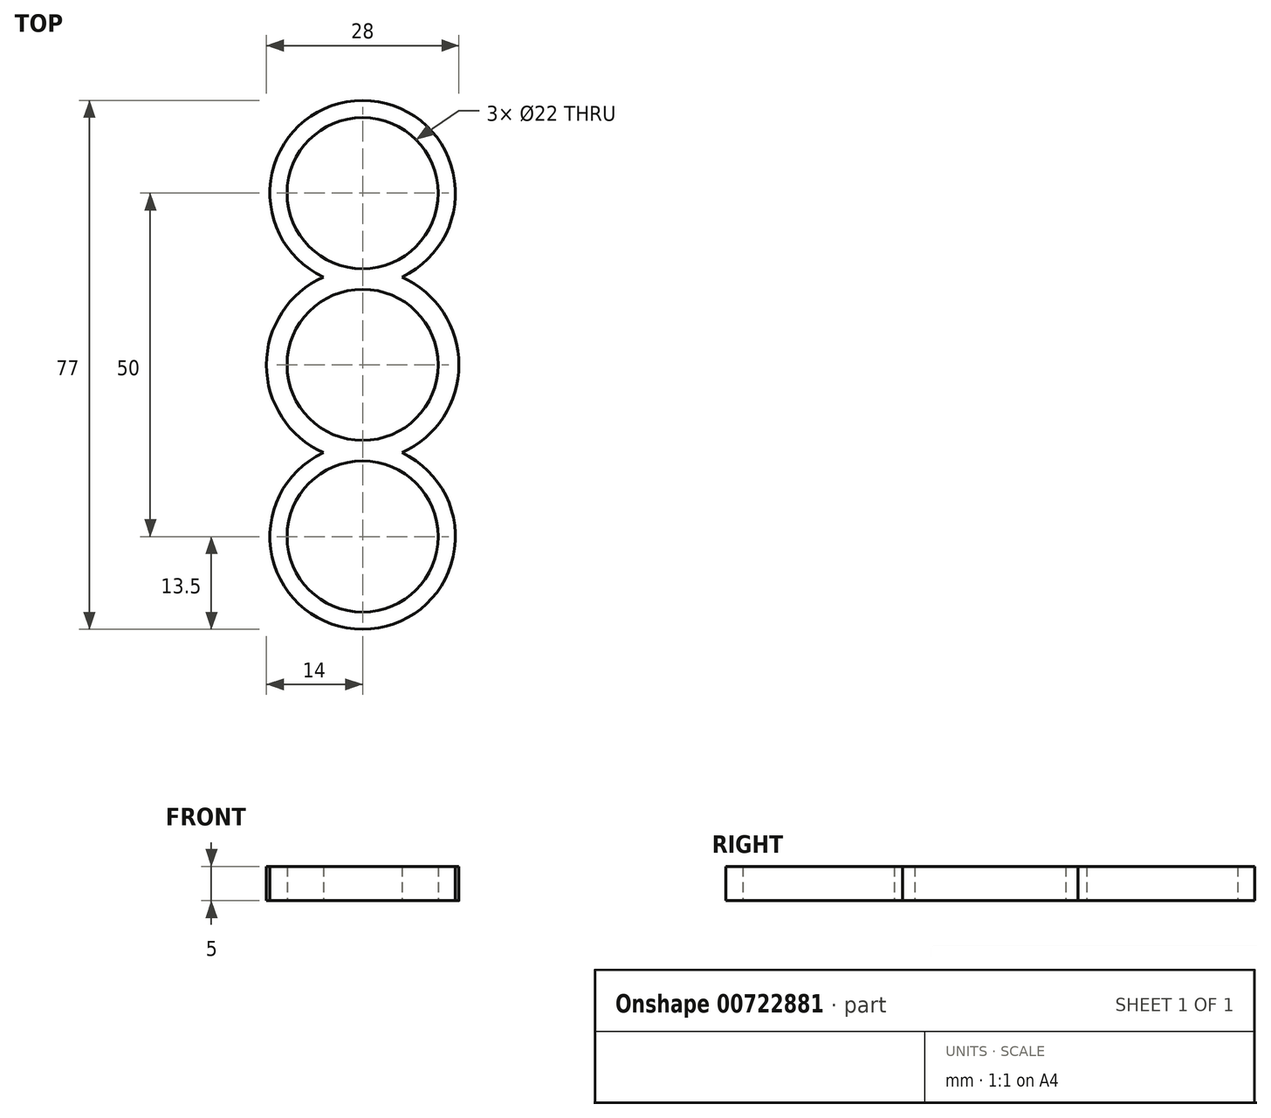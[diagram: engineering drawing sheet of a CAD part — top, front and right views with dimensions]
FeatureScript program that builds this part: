
annotation { "Feature Type Name" : "Feature", "Feature Type Description" : "" }
export const myFeature = defineFeature(function(context is Context, id is Id, definition is map)
    precondition{}
    {
        {
            var Q0;
            Q0=qCreatedBy(makeId("Top.planeOp"),FACE);
            var sketch = newSketch(context, id + "F0", { "sketchPlane" : qUnion([Q0])});
            skCircle(sketch, "E0", {"center": v(0, 0) * mm, "radius": 11 * mm});
            skLineSegment(sketch, "E1", {"start": v(0, 11) * mm, "end": v(0, 14) * mm});
            skCircle(sketch, "E2", {"center": v(0, 25) * mm, "radius": 11 * mm});
            skArc(sketch, "E3", {"start": v(5.73, 12.78) * mm, "mid": v(0, 38.5) * mm, "end": v(-5.73, 12.78) * mm});
            skArc(sketch, "E4", {"start": v(5.73, -12.77) * mm, "mid": v(14, 0) * mm, "end": v(5.73, 12.77) * mm});
            skLineSegment(sketch, "E5", {"start": v(0, -11) * mm, "end": v(0, -14) * mm});
            skCircle(sketch, "E6", {"center": v(0, -25) * mm, "radius": 11 * mm});
            skArc(sketch, "E7", {"start": v(-5.73, -12.78) * mm, "mid": v(0, -38.5) * mm, "end": v(5.73, -12.78) * mm});
            skArc(sketch, "E8.trimOffspring", {"start": v(-5.73, 12.78) * mm, "mid": v(-14, 0) * mm, "end": v(-5.73, -12.78) * mm});
            skSolve(sketch);
        }
        {
            var Q0;
            Q0=makeQuery(id+"F0.imprint","IMPRINT",FACE,{"disambiguationData":[TD([[makeQuery(id+"F0.imprint","IMPRINT",EDGE,{"derivedFrom":sQuery(id+"F0.wireOp",EDGE,"E2")}),-1.0]])]});
            extrude(context, id + "F1", {"entities" : qUnion([Q0]), "depth" : 5 * mm, "offsetDistance" : 25 * mm});
        }
    });
